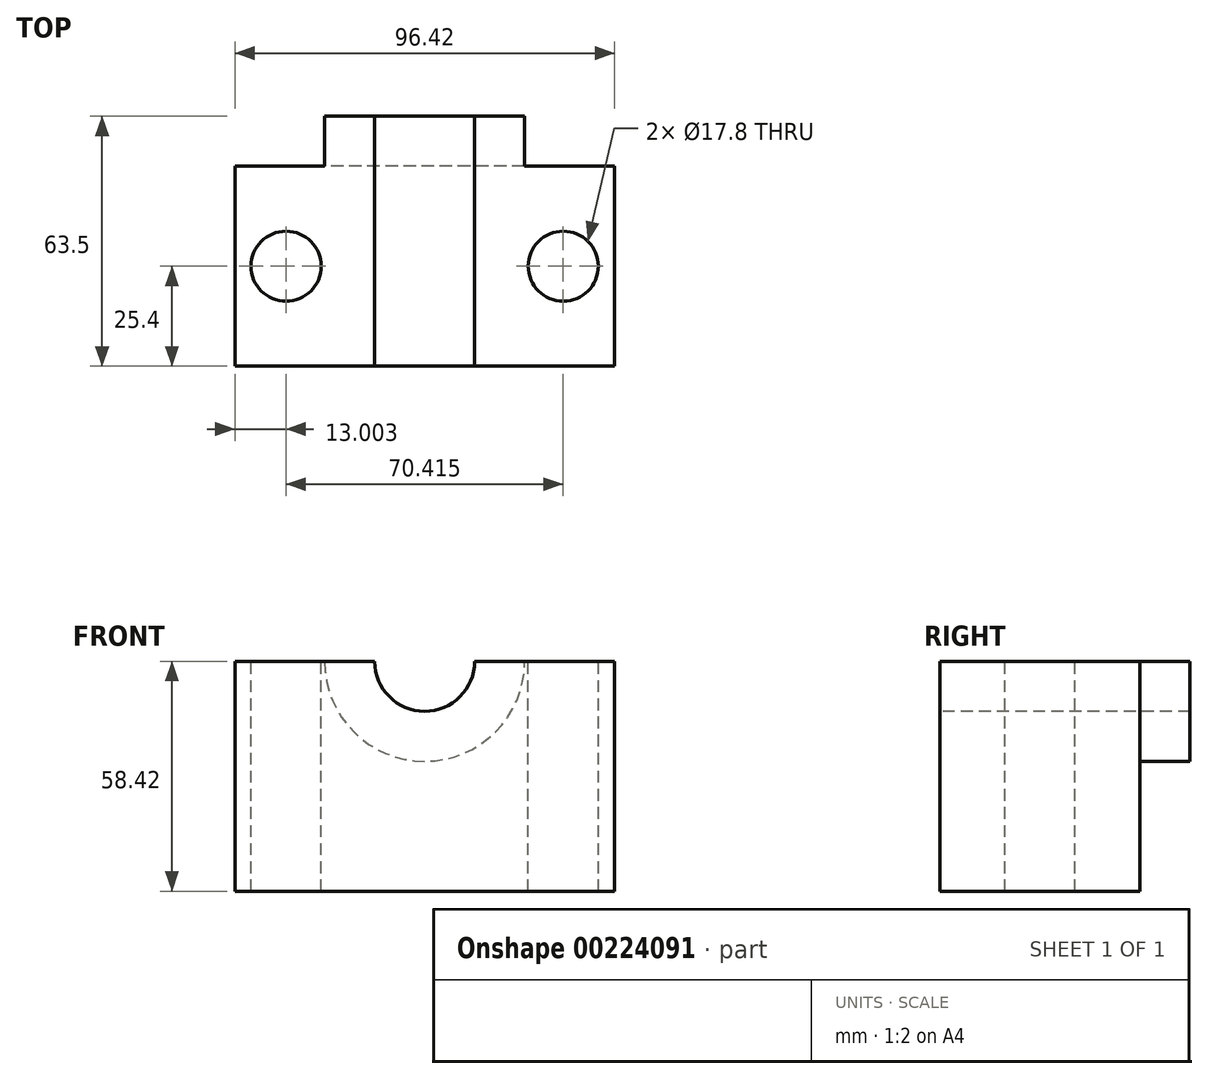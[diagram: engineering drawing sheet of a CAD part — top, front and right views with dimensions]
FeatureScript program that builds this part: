
annotation { "Feature Type Name" : "Feature", "Feature Type Description" : "" }
export const myFeature = defineFeature(function(context is Context, id is Id, definition is map)
    precondition{}
    {
        {
            var Q0;
            Q0=qCreatedBy(makeId("Front.planeOp"),FACE);
            var sketch = newSketch(context, id + "F0", { "sketchPlane" : qUnion([Q0])});
            skLineSegment(sketch, "E0.bottom", {"start": v(48.21, 29.21) * mm, "end": v(-48.21, 29.21) * mm});
            skLineSegment(sketch, "E0.top", {"start": v(48.21, -29.21) * mm, "end": v(-48.21, -29.21) * mm});
            skLineSegment(sketch, "E0.left", {"start": v(48.21, 29.2) * mm, "end": v(48.21, -29.2) * mm});
            skLineSegment(sketch, "E0.right", {"start": v(-48.21, 29.2) * mm, "end": v(-48.21, -29.2) * mm});
            skPoint(sketch, "E0.middle", {"position": v(0, 0) * mm});
            skSolve(sketch);
        }
        {
            var Q0;
            Q0 = qSketchRegion(id + "F0", true);
            extrude(context, id + "F1", {"entities" : qUnion([Q0]), "endBound" : BoundingType.SYMMETRIC, "depth" : 50.8 * mm});
        }
        {
            var Q0;
            Q0=makeQuery(id+"F1.opExtrude","SWEPT_FACE",FACE,{"disambiguationData":[OSD([sQuery(id+"F0.wireOp",EDGE,"E0.bottom")])]});
            var sketch = newSketch(context, id + "F2", { "sketchPlane" : qUnion([Q0])});
            skCircle(sketch, "E1", {"center": v(35.2, 0) * mm, "radius": 8.9 * mm});
            skCircle(sketch, "E2.MirrorC", {"center": v(-35.2, 0) * mm, "radius": 8.9 * mm});
            skSolve(sketch);
        }
        {
            var Q0;
            Q0=makeQuery(id+"F1.opExtrude","CAP_FACE",FACE,{"disambiguationData":[OSD([sQuery(id+"F0.wireOp",EDGE,"E0.bottom"),sQuery(id+"F0.wireOp",EDGE,"E0.top"),sQuery(id+"F0.wireOp",EDGE,"E0.left"),sQuery(id+"F0.wireOp",EDGE,"E0.right")])],"isStart":false});
            var sketch = newSketch(context, id + "F3", { "sketchPlane" : qUnion([Q0])});
            skArc(sketch, "E3", {"start": v(-12.7, 29.21) * mm, "mid": v(0, 16.5) * mm, "end": v(12.7, 29.21) * mm});
            skLineSegment(sketch, "E4", {"start": v(-12.7, 29.21) * mm, "end": v(12.7, 29.21) * mm});
            skSolve(sketch);
        }
        {
            var Q0;
            Q0 = qSketchRegion(id + "F3", true);
            extrude(context, id + "F4", {"entities" : qUnion([Q0]), "operationType" : NewBodyOperationType.REMOVE, "oppositeDirection" : true, "depth" : 254 * mm});
        }
        {
            var Q0;
            Q0=makeQuery(id+"F1.opExtrude","CAP_FACE",FACE,{"disambiguationData":[OSD([sQuery(id+"F0.wireOp",EDGE,"E0.bottom"),sQuery(id+"F0.wireOp",EDGE,"E0.top"),sQuery(id+"F0.wireOp",EDGE,"E0.left"),sQuery(id+"F0.wireOp",EDGE,"E0.right")])],"isStart":true});
            var sketch = newSketch(context, id + "F5", { "sketchPlane" : qUnion([Q0])});
            skArc(sketch, "E5", {"start": v(-25.4, 29.2) * mm, "mid": v(0, 3.8) * mm, "end": v(25.4, 29.21) * mm});
            skLineSegment(sketch, "E6", {"start": v(-25.4, 29.21) * mm, "end": v(-12.7, 29.21) * mm});
            skArc(sketch, "E7", {"start": v(-12.7, 29.21) * mm, "mid": v(0, 16.5) * mm, "end": v(12.7, 29.21) * mm});
            skLineSegment(sketch, "E8.trimOffspring", {"start": v(12.7, 29.21) * mm, "end": v(25.4, 29.21) * mm});
            skSolve(sketch);
        }
        {
            var Q0;
            Q0 = qSketchRegion(id + "F5", true);
            extrude(context, id + "F6", {"entities" : qUnion([Q0]), "operationType" : NewBodyOperationType.ADD, "depth" : 12.7 * mm});
        }
        {
            var Q0;
            Q0 = qSketchRegion(id + "F2", true);
            extrude(context, id + "F7", {"entities" : qUnion([Q0]), "operationType" : NewBodyOperationType.REMOVE, "oppositeDirection" : true, "depth" : 254 * mm});
        }
    });
